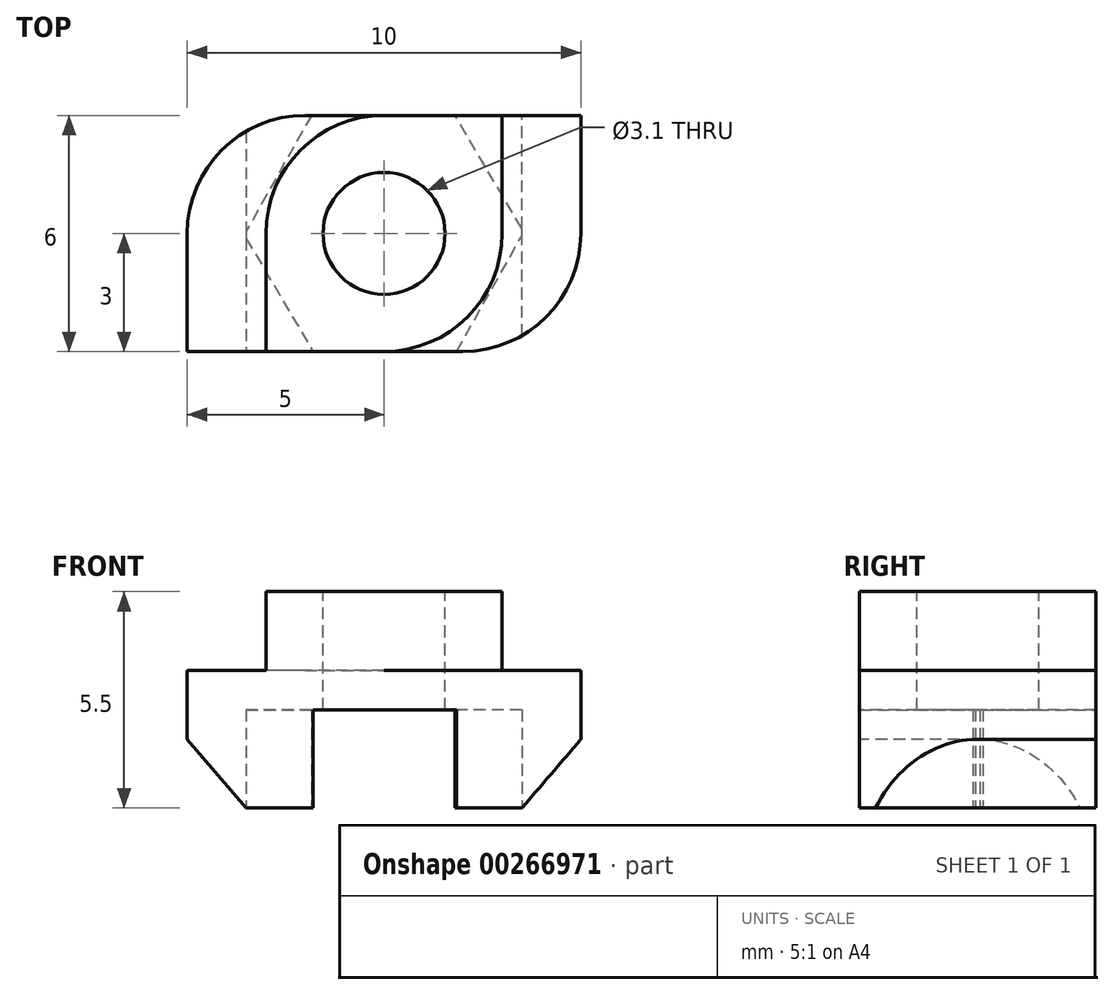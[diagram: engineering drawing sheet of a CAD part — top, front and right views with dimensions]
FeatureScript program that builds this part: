
annotation { "Feature Type Name" : "Feature", "Feature Type Description" : "" }
export const myFeature = defineFeature(function(context is Context, id is Id, definition is map)
    precondition{}
    {
        {
            var Q0;
            Q0=qCreatedBy(makeId("Top.planeOp"),FACE);
            var sketch = newSketch(context, id + "F0", { "sketchPlane" : qUnion([Q0])});
            skLineSegment(sketch, "E0.bottom", {"start": v(-5, -3) * mm, "end": v(2, -3) * mm});
            skLineSegment(sketch, "E0.top", {"start": v(-2, 3) * mm, "end": v(5, 3) * mm});
            skLineSegment(sketch, "E0.left", {"start": v(-5, -3) * mm, "end": v(-5, 0) * mm});
            skLineSegment(sketch, "E0.right", {"start": v(5, 0) * mm, "end": v(5, 3) * mm});
            skPoint(sketch, "E0.middle", {"position": v(0, 0) * mm});
            skArc(sketch, "E1", {"start": v(-2, 3) * mm, "mid": v(-4.12, 2.12) * mm, "end": v(-5, 0) * mm});
            skArc(sketch, "E2", {"start": v(2, -3) * mm, "mid": v(4.12, -2.12) * mm, "end": v(5, 0) * mm});
            skPoint(sketch, "E3.orphan", {"position": v(-5, 3) * mm});
            skPoint(sketch, "E4.orphan", {"position": v(5, -3) * mm});
            skSolve(sketch);
        }
        {
            var Q0;
            Q0=qSketchRegion(id+"F0",true);
            extrude(context, id + "F1", {"entities" : qUnion([Q0]), "depth" : 3.5 * mm});
        }
        {
            var Q0;
            Q0=makeQuery(id+"F1.opExtrude","CAP_FACE",FACE,{"disambiguationData":[OSD([sQuery(id+"F0.wireOp",EDGE,"E0.bottom"),sQuery(id+"F0.wireOp",EDGE,"E0.top"),sQuery(id+"F0.wireOp",EDGE,"E0.left"),sQuery(id+"F0.wireOp",EDGE,"E0.right"),sQuery(id+"F0.wireOp",EDGE,"E1"),sQuery(id+"F0.wireOp",EDGE,"E2")])],"isStart":false});
            var sketch = newSketch(context, id + "F2", { "sketchPlane" : qUnion([Q0])});
            skLineSegment(sketch, "E5.bottom", {"start": v(3, 3) * mm, "end": v(0, 3) * mm});
            skLineSegment(sketch, "E5.top", {"start": v(0, -3) * mm, "end": v(-3, -3) * mm});
            skLineSegment(sketch, "E5.left", {"start": v(3, 3) * mm, "end": v(3, 0) * mm});
            skLineSegment(sketch, "E5.right", {"start": v(-3, 0) * mm, "end": v(-3, -3) * mm});
            skPoint(sketch, "E5.middle", {"position": v(0, 0) * mm});
            skArc(sketch, "E6", {"start": v(0, -3) * mm, "mid": v(2.12, -2.12) * mm, "end": v(3, 0) * mm});
            skPoint(sketch, "E7.orphan", {"position": v(-3, 3) * mm});
            skPoint(sketch, "E8.orphan", {"position": v(3, -3) * mm});
            skArc(sketch, "E9.trimOffspring", {"start": v(0, 3) * mm, "mid": v(-2.12, 2.12) * mm, "end": v(-3, 0) * mm});
            skSolve(sketch);
        }
        {
            var Q0;
            Q0=makeQuery(id+"F2.imprint","IMPRINT",FACE,{"disambiguationData":[TD([[makeQuery(id+"F2.imprint","IMPRINT",EDGE,{"derivedFrom":sQuery(id+"F2.wireOp",EDGE,"E5.bottom")}),-1.0]])]});
            extrude(context, id + "F3", {"entities" : qUnion([Q0]), "operationType" : NewBodyOperationType.ADD, "depth" : 2 * mm});
        }
        {
            var Q0;
            Q0=makeQuery(id+"F3.opExtrude","CAP_FACE",FACE,{"disambiguationData":[OSD([sQuery(id+"F2.wireOp",EDGE,"E5.bottom"),sQuery(id+"F2.wireOp",EDGE,"E5.top"),sQuery(id+"F2.wireOp",EDGE,"E5.left"),sQuery(id+"F2.wireOp",EDGE,"E5.right"),sQuery(id+"F2.wireOp",EDGE,"E6"),sQuery(id+"F2.wireOp",EDGE,"E9.trimOffspring")])],"isStart":false});
            var sketch = newSketch(context, id + "F4", { "sketchPlane" : qUnion([Q0])});
            skCircle(sketch, "E10", {"center": v(0, 0) * mm, "radius": 1.55 * mm});
            skSolve(sketch);
        }
        {
            var Q0;
            Q0=qSketchRegion(id+"F4",true);
            extrude(context, id + "F5", {"entities" : qUnion([Q0]), "operationType" : NewBodyOperationType.REMOVE, "oppositeDirection" : true, "depth" : 25 * mm});
        }
        {
            var Q0;
            Q0=makeQuery(id+"F3.boolean.opBoolean","MERGE",FACE,{"derivedFrom":[makeQuery(id+"F1.opExtrude","SWEPT_FACE",FACE,{"disambiguationData":[OSD([sQuery(id+"F0.wireOp",EDGE,"E0.bottom")])]}),makeQuery(id+"F3.opExtrude","SWEPT_FACE",FACE,{"disambiguationData":[OSD([sQuery(id+"F2.wireOp",EDGE,"E5.top")])]})]});
            var sketch = newSketch(context, id + "F6", { "sketchPlane" : qUnion([Q0])});
            skLineSegment(sketch, "E11", {"start": v(-5, 1.75) * mm, "end": v(-3.5, 0) * mm});
            skLineSegment(sketch, "E12", {"start": v(-3.5, 0) * mm, "end": v(-5, 0) * mm});
            skLineSegment(sketch, "E13", {"start": v(-5, 0) * mm, "end": v(-5, 1.75) * mm});
            skSolve(sketch);
        }
        {
            var Q0;
            Q0=makeQuery(id+"F6.imprint","IMPRINT",FACE,{"disambiguationData":[TD([[makeQuery(id+"F6.imprint","IMPRINT",EDGE,{"derivedFrom":sQuery(id+"F6.wireOp",EDGE,"E11")}),-1.0]])]});
            extrude(context, id + "F7", {"entities" : qUnion([Q0]), "operationType" : NewBodyOperationType.REMOVE, "oppositeDirection" : true, "depth" : 25 * mm});
        }
        {
            var Q0;
            Q0=makeQuery(id+"F3.boolean.opBoolean","MERGE",FACE,{"derivedFrom":[makeQuery(id+"F1.opExtrude","SWEPT_FACE",FACE,{"disambiguationData":[OSD([sQuery(id+"F0.wireOp",EDGE,"E0.top")])]}),makeQuery(id+"F3.opExtrude","SWEPT_FACE",FACE,{"disambiguationData":[OSD([sQuery(id+"F2.wireOp",EDGE,"E5.bottom")])]})]});
            var sketch = newSketch(context, id + "F8", { "sketchPlane" : qUnion([Q0])});
            skLineSegment(sketch, "E14", {"start": v(-3.5, 0) * mm, "end": v(-5, 0) * mm});
            skLineSegment(sketch, "E15", {"start": v(-5, 0) * mm, "end": v(-5, 1.75) * mm});
            skLineSegment(sketch, "E16", {"start": v(-5, 1.75) * mm, "end": v(-3.5, 0) * mm});
            skSolve(sketch);
        }
        {
            var Q0;
            Q0=makeQuery(id+"F8.imprint","IMPRINT",FACE,{"disambiguationData":[TD([[makeQuery(id+"F8.imprint","IMPRINT",EDGE,{"derivedFrom":sQuery(id+"F8.wireOp",EDGE,"E14")}),-1.0]])]});
            extrude(context, id + "F9", {"entities" : qUnion([Q0]), "operationType" : NewBodyOperationType.REMOVE, "oppositeDirection" : true, "depth" : 25 * mm});
        }
        {
            var Q0;
            Q0=makeQuery(id+"F1.opExtrude","CAP_FACE",FACE,{"disambiguationData":[OSD([sQuery(id+"F0.wireOp",EDGE,"E0.bottom"),sQuery(id+"F0.wireOp",EDGE,"E0.top"),sQuery(id+"F0.wireOp",EDGE,"E0.left"),sQuery(id+"F0.wireOp",EDGE,"E0.right"),sQuery(id+"F0.wireOp",EDGE,"E1"),sQuery(id+"F0.wireOp",EDGE,"E2")])],"isStart":true});
            var sketch = newSketch(context, id + "F10", { "sketchPlane" : qUnion([Q0])});
            skCircle(sketch, "E17.cCircle", {"center": v(0, 0) * mm, "radius": 3.08 * mm, "construction": true});
            skLineSegment(sketch, "E17.0", {"start": v(3.55, -0.04) * mm, "end": v(1.75, -3.1) * mm});
            skLineSegment(sketch, "E17.1", {"start": v(1.75, -3.1) * mm, "end": v(-1.8, -3.06) * mm});
            skLineSegment(sketch, "E17.2", {"start": v(-1.8, -3.06) * mm, "end": v(-3.55, 0.04) * mm});
            skLineSegment(sketch, "E17.3", {"start": v(-3.55, 0.04) * mm, "end": v(-1.75, 3.1) * mm});
            skLineSegment(sketch, "E17.4", {"start": v(-1.75, 3.1) * mm, "end": v(1.8, 3.06) * mm});
            skLineSegment(sketch, "E17.5", {"start": v(1.8, 3.06) * mm, "end": v(3.55, -0.04) * mm});
            skPoint(sketch, "E17.0.midPoint", {"position": v(2.65, -1.57) * mm});
            skSolve(sketch);
        }
        {
            var Q0;
            {var subQ1=sQuery(id+"F0.wireOp",EDGE,"E0.bottom");var subQ2=makeQuery(id+"F1.opExtrude","CAP_EDGE",EDGE,{"disambiguationData":[OSD([subQ1])],"isStart":true});var subQ10=sQuery(id+"F10.wireOp",EDGE,"E17.3");var subQ14=makeQuery(id+"F10.imprint","INTERSECT",VERTEX,{"derivedFrom":[subQ2,subQ10]});Q0=makeQuery(id+"F10.imprint","IMPRINT",FACE,{"disambiguationData":[TD([[makeQuery(id+"F10.imprint","IMPRINT",EDGE,{"disambiguationData":[TD([[subQ14,-1.0]])],"derivedFrom":subQ2}),-1.0]])]});}
            extrude(context, id + "F11", {"entities" : qUnion([Q0]), "operationType" : NewBodyOperationType.REMOVE, "oppositeDirection" : true, "depth" : 2.5 * mm});
        }
    });
